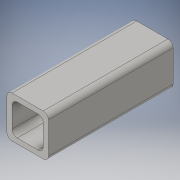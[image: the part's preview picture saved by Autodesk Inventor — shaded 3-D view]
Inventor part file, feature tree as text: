
AUTODESK INVENTOR PART (.ipt)
format: ipt  version: 2016 (Build 200138000, 138)  size: 111,104 bytes
history: native  units: in
note: dims shown in document units (in); Inventor stores cm internally (conversion verified against a paired STEP export)
features: extrude x1, sketch x1
ambient origin geometry x8: Origin, YZ Plane, XZ Plane, XY Plane, X Axis, Y Axis, Z Axis, Center Point
bodies: Solid1 (feature_tree)
feature tree (2):
  extrude  "Extrusion1"  Depth=1.0in
  sketch  "Sketch1"  dims[d0=1.0in d1=1.0in d2=0.125in d3=0.125in d4=3.0in d5=0.0in]
